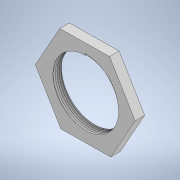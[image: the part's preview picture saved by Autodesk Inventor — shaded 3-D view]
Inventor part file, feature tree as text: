
AUTODESK INVENTOR PART (.ipt)
format: ipt  version: 2022.2 (Build 262287030, 287C)  size: 274,432 bytes
history: native  units: in
note: dims shown in document units (in); Inventor stores cm internally (conversion verified against a paired STEP export)
features: extrude x1, helix x1, sketch x1
ambient origin geometry x8: Origin, YZ Plane, XZ Plane, XY Plane, X Axis, Y Axis, Z Axis, Center Point
bodies: Solid1 (feature_tree)
feature tree (3):
  extrude  "Extrusion1"  Depth=0.1969in TaperAngle=0.0deg
  helix  "Coil1"  [1 undecoded]
  sketch  "Sketch2"  dims[d0=1.3358in d2=0.1969in d3=0.0in d4=0.0401in d5=0.0394in d6=0.6679in d7=0.0039in d8=0.0in d9=0.0394in d10=0.3937in d11=3.1496in d12=0.0in d13=90.0deg d14=90.0deg d15=0.0in d16=0.0in]
note: 1 required parameter value undecoded (feature->parameter linkage not recoverable at this tier; creation-order binding heuristic only, values carry confidence <= 0.55)
